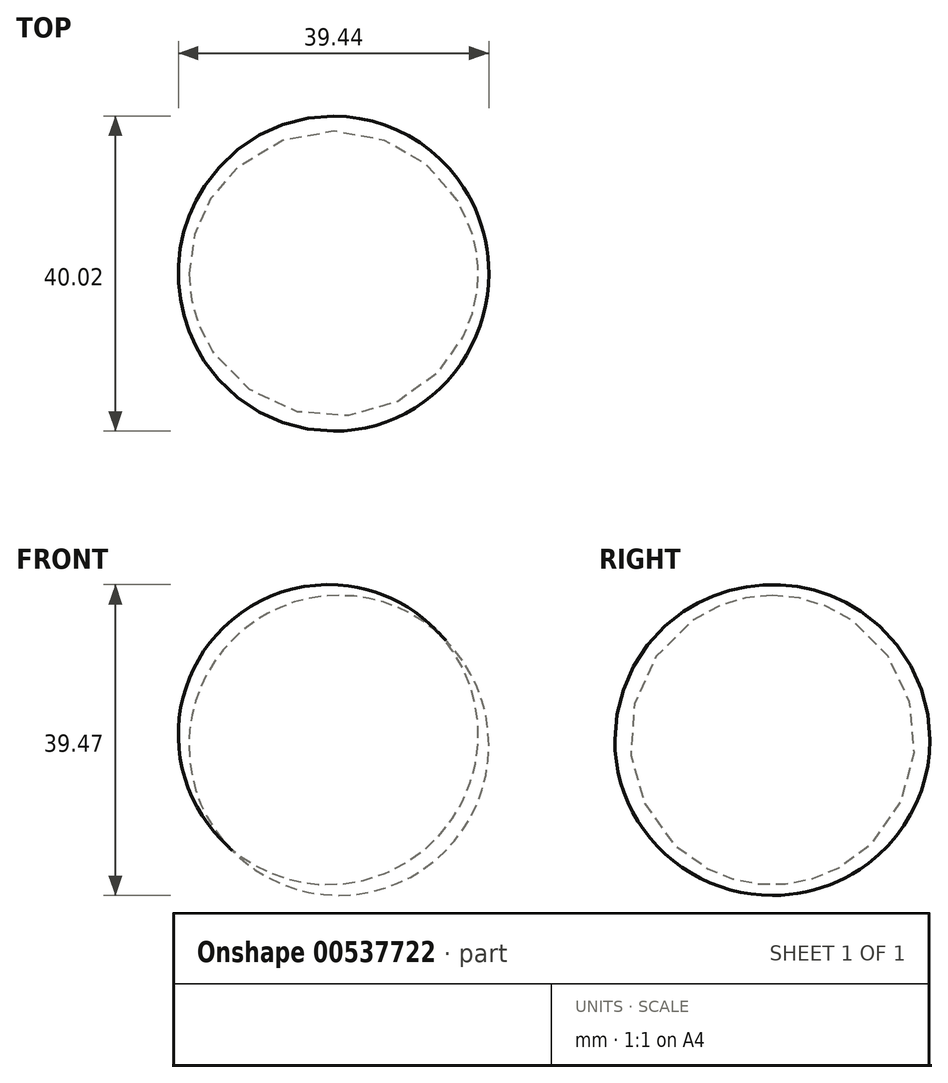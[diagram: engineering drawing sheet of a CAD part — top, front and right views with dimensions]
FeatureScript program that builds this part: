
annotation { "Feature Type Name" : "Feature", "Feature Type Description" : "" }
export const myFeature = defineFeature(function(context is Context, id is Id, definition is map)
    precondition{}
    {
        {
            var Q0;
            Q0=qCreatedBy(makeId("Front.planeOp"),FACE);
            var sketch = newSketch(context, id + "F0", { "sketchPlane" : qUnion([Q0])});
            skArc(sketch, "E0", {"start": v(-14.27, -12.63) * mm, "mid": v(13.33, -13.61) * mm, "end": v(12.92, 14) * mm});
            skLineSegment(sketch, "E1", {"start": v(12.92, 14) * mm, "end": v(-14.27, -12.63) * mm});
            skSolve(sketch);
        }
        {
            var Q0;
            Q0=makeQuery(id+"F0.imprint","IMPRINT",FACE,{"disambiguationData":[TD([[makeQuery(id+"F0.imprint","IMPRINT",EDGE,{"derivedFrom":sQuery(id+"F0.wireOp",EDGE,"E0")}),1.0]])]});
            var Q1;
            Q1=sQuery(id+"F0.wireOp",EDGE,"E1");
            revolve(context, id + "F1", {"entities" : qUnion([Q0]), "axis" : qUnion([Q1]), "revolveType" : RevolveType.FULL});
        }
    });
